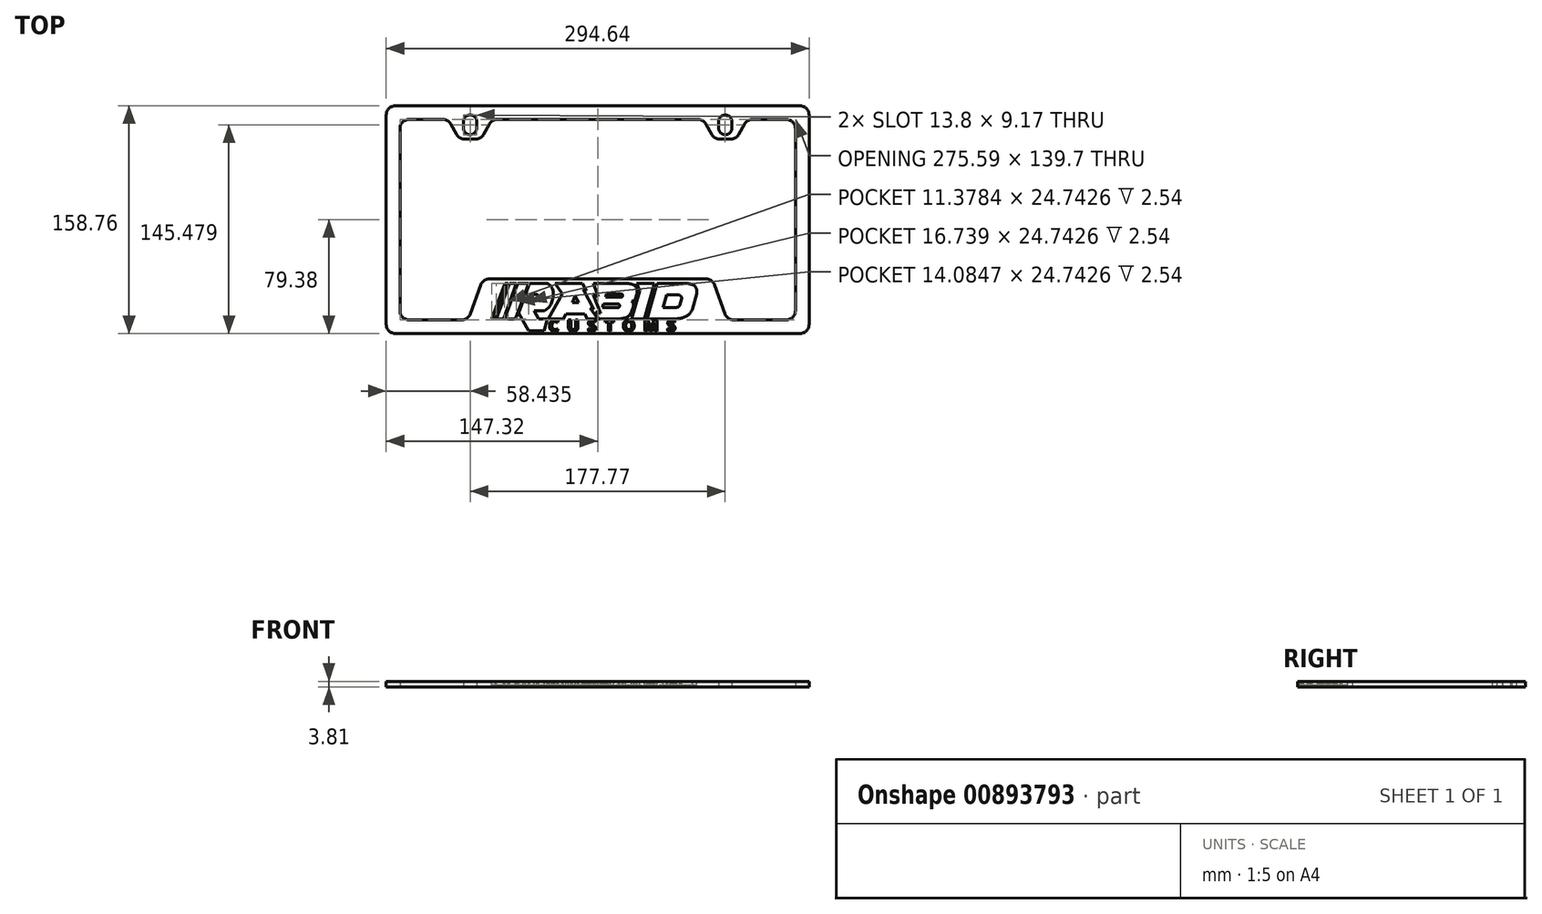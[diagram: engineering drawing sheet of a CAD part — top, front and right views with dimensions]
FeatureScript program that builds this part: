
annotation { "Feature Type Name" : "Feature", "Feature Type Description" : "" }
export const myFeature = defineFeature(function(context is Context, id is Id, definition is map)
    precondition{}
    {
        {
            var Q0;
            Q0=qCreatedBy(makeId("Top.planeOp"),FACE);
            var sketch = newSketch(context, id + "F0", { "sketchPlane" : qUnion([Q0])});
            skLineSegment(sketch, "E0.bottom", {"start": v(-140.97, 79.38) * mm, "end": v(140.97, 79.38) * mm});
            skLineSegment(sketch, "E0.top", {"start": v(-140.97, -79.38) * mm, "end": v(140.97, -79.38) * mm});
            skLineSegment(sketch, "E0.left", {"start": v(-147.32, 73.03) * mm, "end": v(-147.32, -73.03) * mm});
            skLineSegment(sketch, "E0.right", {"start": v(147.32, 73.03) * mm, "end": v(147.32, -73.03) * mm});
            skLineSegment(sketch, "E1.bottom", {"start": v(-131.44, 69.85) * mm, "end": v(-107.87, 69.85) * mm});
            skLineSegment(sketch, "E1.top", {"start": v(-131.44, -69.85) * mm, "end": v(-94.65, -69.85) * mm});
            skLineSegment(sketch, "E1.left", {"start": v(-137.8, 63.5) * mm, "end": v(-137.8, -63.5) * mm});
            skLineSegment(sketch, "E1.right", {"start": v(137.8, 63.5) * mm, "end": v(137.8, -63.5) * mm});
            skLineSegment(sketch, "E2", {"start": v(-102.32, 66.6) * mm, "end": v(-98.34, 59.44) * mm});
            skLineSegment(sketch, "E3", {"start": v(-92.8, 56.19) * mm, "end": v(-85, 56.19) * mm});
            skLineSegment(sketch, "E4", {"start": v(-79.46, 59.44) * mm, "end": v(-75.48, 66.6) * mm});
            skLineSegment(sketch, "E5.trimOffspring", {"start": v(-69.93, 69.85) * mm, "end": v(69.93, 69.85) * mm});
            skArc(sketch, "E6", {"start": v(-84.3, 68.68) * mm, "mid": v(-88.47, 73) * mm, "end": v(-93.37, 69.54) * mm});
            skArc(sketch, "E7", {"start": v(-93.47, 63.22) * mm, "mid": v(-88.82, 59.2) * mm, "end": v(-84.31, 63.37) * mm});
            skLineSegment(sketch, "E8", {"start": v(-93.37, 69.54) * mm, "end": v(-93.47, 63.22) * mm});
            skLineSegment(sketch, "E9", {"start": v(-84.3, 68.68) * mm, "end": v(-84.31, 63.37) * mm});
            skLineSegment(sketch, "E10.MirrorCS", {"start": v(84.3, 68.68) * mm, "end": v(84.31, 63.37) * mm});
            skLineSegment(sketch, "E11.MirrorCS", {"start": v(93.37, 69.54) * mm, "end": v(93.47, 63.22) * mm});
            skLineSegment(sketch, "E12.MirrorCS", {"start": v(102.32, 66.6) * mm, "end": v(98.34, 59.44) * mm});
            skLineSegment(sketch, "E13.MirrorCS", {"start": v(92.8, 56.19) * mm, "end": v(85, 56.19) * mm});
            skLineSegment(sketch, "E14.MirrorCS", {"start": v(79.46, 59.44) * mm, "end": v(75.48, 66.6) * mm});
            skArc(sketch, "E15.MirrorCS", {"start": v(93.47, 63.22) * mm, "mid": v(88.82, 59.2) * mm, "end": v(84.31, 63.37) * mm});
            skArc(sketch, "E16.MirrorCS", {"start": v(84.3, 68.68) * mm, "mid": v(88.47, 73) * mm, "end": v(93.37, 69.54) * mm});
            skLineSegment(sketch, "E17.trimOffspring", {"start": v(107.87, 69.85) * mm, "end": v(131.44, 69.85) * mm});
            skPoint(sketch, "E18.visualSharp", {"position": v(-137.8, 69.85) * mm});
            skArc(sketch, "E18.filletArc", {"start": v(-131.44, 69.85) * mm, "mid": v(-135.94, 68) * mm, "end": v(-137.8, 63.5) * mm});
            skPoint(sketch, "E19.visualSharp", {"position": v(-147.32, 79.38) * mm});
            skArc(sketch, "E19.filletArc", {"start": v(-140.97, 79.37) * mm, "mid": v(-145.46, 77.52) * mm, "end": v(-147.32, 73.03) * mm});
            skPoint(sketch, "E20.visualSharp", {"position": v(137.8, 69.85) * mm});
            skArc(sketch, "E20.filletArc", {"start": v(137.8, 63.5) * mm, "mid": v(135.94, 68) * mm, "end": v(131.44, 69.85) * mm});
            skPoint(sketch, "E21.visualSharp", {"position": v(147.32, 79.38) * mm});
            skArc(sketch, "E21.filletArc", {"start": v(147.32, 73.03) * mm, "mid": v(145.46, 77.52) * mm, "end": v(140.97, 79.38) * mm});
            skPoint(sketch, "E22.visualSharp", {"position": v(147.32, -79.38) * mm});
            skArc(sketch, "E22.filletArc", {"start": v(140.97, -79.37) * mm, "mid": v(145.46, -77.52) * mm, "end": v(147.32, -73.03) * mm});
            skPoint(sketch, "E23.visualSharp", {"position": v(137.8, -69.85) * mm});
            skArc(sketch, "E23.filletArc", {"start": v(131.44, -69.85) * mm, "mid": v(135.94, -68) * mm, "end": v(137.8, -63.5) * mm});
            skPoint(sketch, "E24.visualSharp", {"position": v(-147.32, -79.38) * mm});
            skArc(sketch, "E24.filletArc", {"start": v(-147.32, -73.03) * mm, "mid": v(-145.46, -77.52) * mm, "end": v(-140.97, -79.38) * mm});
            skPoint(sketch, "E25.visualSharp", {"position": v(-137.8, -69.85) * mm});
            skArc(sketch, "E25.filletArc", {"start": v(-137.8, -63.5) * mm, "mid": v(-135.94, -68) * mm, "end": v(-131.44, -69.85) * mm});
            skLineSegment(sketch, "E26", {"start": v(-88.67, -65.63) * mm, "end": v(-81.51, -45.5) * mm});
            skLineSegment(sketch, "E27", {"start": v(-75.53, -41.27) * mm, "end": v(75.53, -41.27) * mm});
            skLineSegment(sketch, "E28", {"start": v(81.51, -45.5) * mm, "end": v(88.67, -65.63) * mm});
            skLineSegment(sketch, "E29.trimOffspring", {"start": v(94.65, -69.85) * mm, "end": v(131.44, -69.85) * mm});
            skPoint(sketch, "E30.visualSharp", {"position": v(-104.14, 69.85) * mm});
            skArc(sketch, "E30.filletArc", {"start": v(-102.32, 66.6) * mm, "mid": v(-104.65, 68.98) * mm, "end": v(-107.87, 69.85) * mm});
            skPoint(sketch, "E31.visualSharp", {"position": v(-96.52, 56.19) * mm});
            skArc(sketch, "E31.filletArc", {"start": v(-98.34, 59.44) * mm, "mid": v(-96, 57.06) * mm, "end": v(-92.8, 56.19) * mm});
            skPoint(sketch, "E32.visualSharp", {"position": v(-81.28, 56.19) * mm});
            skArc(sketch, "E32.filletArc", {"start": v(-85, 56.19) * mm, "mid": v(-81.8, 57.06) * mm, "end": v(-79.46, 59.44) * mm});
            skPoint(sketch, "E33.visualSharp", {"position": v(-73.66, 69.85) * mm});
            skArc(sketch, "E33.filletArc", {"start": v(-69.93, 69.85) * mm, "mid": v(-73.15, 68.98) * mm, "end": v(-75.48, 66.6) * mm});
            skPoint(sketch, "E34.visualSharp", {"position": v(104.14, 69.85) * mm});
            skArc(sketch, "E34.filletArc", {"start": v(107.87, 69.85) * mm, "mid": v(104.65, 68.98) * mm, "end": v(102.32, 66.6) * mm});
            skPoint(sketch, "E35.visualSharp", {"position": v(96.52, 56.19) * mm});
            skArc(sketch, "E35.filletArc", {"start": v(92.8, 56.19) * mm, "mid": v(96, 57.06) * mm, "end": v(98.34, 59.44) * mm});
            skPoint(sketch, "E36.visualSharp", {"position": v(81.28, 56.19) * mm});
            skArc(sketch, "E36.filletArc", {"start": v(79.46, 59.44) * mm, "mid": v(81.8, 57.06) * mm, "end": v(85, 56.19) * mm});
            skPoint(sketch, "E37.visualSharp", {"position": v(73.66, 69.85) * mm});
            skArc(sketch, "E37.filletArc", {"start": v(75.48, 66.6) * mm, "mid": v(73.15, 68.98) * mm, "end": v(69.93, 69.85) * mm});
            skPoint(sketch, "E38.visualSharp", {"position": v(90.17, -69.85) * mm});
            skArc(sketch, "E38.filletArc", {"start": v(88.67, -65.63) * mm, "mid": v(91, -68.69) * mm, "end": v(94.65, -69.85) * mm});
            skPoint(sketch, "E39.visualSharp", {"position": v(80, -41.27) * mm});
            skArc(sketch, "E39.filletArc", {"start": v(81.51, -45.5) * mm, "mid": v(79.19, -42.44) * mm, "end": v(75.53, -41.27) * mm});
            skPoint(sketch, "E40.visualSharp", {"position": v(-80, -41.27) * mm});
            skArc(sketch, "E40.filletArc", {"start": v(-75.53, -41.27) * mm, "mid": v(-79.19, -42.44) * mm, "end": v(-81.51, -45.5) * mm});
            skPoint(sketch, "E41.visualSharp", {"position": v(-90.17, -69.85) * mm});
            skArc(sketch, "E41.filletArc", {"start": v(-94.65, -69.85) * mm, "mid": v(-91, -68.69) * mm, "end": v(-88.67, -65.63) * mm});
            skSolve(sketch);
        }
        {
            var Q0;
            Q0 = qSketchRegion(id + "F0", true);
            extrude(context, id + "F1", {"entities" : qUnion([Q0]), "depth" : 3.8 * mm, "offsetDistance" : 25.4 * mm});
        }
        {
            var Q0;
            Q0=makeQuery(id+"F1.opExtrude","CAP_FACE",FACE,{"disambiguationData":[OSD([sQuery(id+"F0.wireOp",EDGE,"E0.bottom"),sQuery(id+"F0.wireOp",EDGE,"E0.top"),sQuery(id+"F0.wireOp",EDGE,"E0.left"),sQuery(id+"F0.wireOp",EDGE,"E0.right"),sQuery(id+"F0.wireOp",EDGE,"E1.bottom"),sQuery(id+"F0.wireOp",EDGE,"E1.top"),sQuery(id+"F0.wireOp",EDGE,"E1.left"),sQuery(id+"F0.wireOp",EDGE,"E1.right"),sQuery(id+"F0.wireOp",EDGE,"E2"),sQuery(id+"F0.wireOp",EDGE,"E3"),sQuery(id+"F0.wireOp",EDGE,"E4"),sQuery(id+"F0.wireOp",EDGE,"E5.trimOffspring"),sQuery(id+"F0.wireOp",EDGE,"E6"),sQuery(id+"F0.wireOp",EDGE,"E7"),sQuery(id+"F0.wireOp",EDGE,"E8"),sQuery(id+"F0.wireOp",EDGE,"E9"),sQuery(id+"F0.wireOp",EDGE,"E10.MirrorCS"),sQuery(id+"F0.wireOp",EDGE,"E11.MirrorCS"),sQuery(id+"F0.wireOp",EDGE,"E12.MirrorCS"),sQuery(id+"F0.wireOp",EDGE,"E13.MirrorCS"),sQuery(id+"F0.wireOp",EDGE,"E14.MirrorCS"),sQuery(id+"F0.wireOp",EDGE,"E15.MirrorCS"),sQuery(id+"F0.wireOp",EDGE,"E16.MirrorCS"),sQuery(id+"F0.wireOp",EDGE,"E17.trimOffspring"),sQuery(id+"F0.wireOp",EDGE,"E18.filletArc"),sQuery(id+"F0.wireOp",EDGE,"E19.filletArc"),sQuery(id+"F0.wireOp",EDGE,"E20.filletArc"),sQuery(id+"F0.wireOp",EDGE,"E21.filletArc"),sQuery(id+"F0.wireOp",EDGE,"E22.filletArc"),sQuery(id+"F0.wireOp",EDGE,"E23.filletArc"),sQuery(id+"F0.wireOp",EDGE,"E24.filletArc"),sQuery(id+"F0.wireOp",EDGE,"E25.filletArc"),sQuery(id+"F0.wireOp",EDGE,"E26"),sQuery(id+"F0.wireOp",EDGE,"E27"),sQuery(id+"F0.wireOp",EDGE,"E28"),sQuery(id+"F0.wireOp",EDGE,"E29.trimOffspring"),sQuery(id+"F0.wireOp",EDGE,"E30.filletArc"),sQuery(id+"F0.wireOp",EDGE,"E31.filletArc"),sQuery(id+"F0.wireOp",EDGE,"E32.filletArc"),sQuery(id+"F0.wireOp",EDGE,"E33.filletArc"),sQuery(id+"F0.wireOp",EDGE,"E34.filletArc"),sQuery(id+"F0.wireOp",EDGE,"E35.filletArc"),sQuery(id+"F0.wireOp",EDGE,"E36.filletArc"),sQuery(id+"F0.wireOp",EDGE,"E37.filletArc"),sQuery(id+"F0.wireOp",EDGE,"E38.filletArc"),sQuery(id+"F0.wireOp",EDGE,"E39.filletArc"),sQuery(id+"F0.wireOp",EDGE,"E40.filletArc"),sQuery(id+"F0.wireOp",EDGE,"E41.filletArc")])],"isStart":false});
            var sketch = newSketch(context, id + "F2", { "sketchPlane" : qUnion([Q0])});
            skLineSegment(sketch, "E42", {"start": v(61.7, -44.47) * mm, "end": v(41.47, -44.47) * mm});
            skLineSegment(sketch, "E43", {"start": v(-73.67, -69.2) * mm, "end": v(-64.57, -44.47) * mm});
            skLineSegment(sketch, "E44", {"start": v(-57.33, -69.2) * mm, "end": v(-64.96, -69.2) * mm});
            skLineSegment(sketch, "E45", {"start": v(-62.3, -44.47) * mm, "end": v(-71.4, -69.2) * mm});
            skLineSegment(sketch, "E46", {"start": v(-70.7, -69.2) * mm, "end": v(-61.59, -44.47) * mm});
            skLineSegment(sketch, "E47", {"start": v(-56.6, -44.47) * mm, "end": v(-65.71, -69.2) * mm});
            skLineSegment(sketch, "E48", {"start": v(-64.96, -69.2) * mm, "end": v(-55.86, -44.47) * mm});
            skLineSegment(sketch, "E49", {"start": v(-48.22, -44.47) * mm, "end": v(-57.33, -69.2) * mm});
            skLineSegment(sketch, "E50", {"start": v(-50.37, -52.19) * mm, "end": v(-47.53, -44.47) * mm});
            skLineSegment(sketch, "E51", {"start": v(-50.37, -52.19) * mm, "end": v(-42.1, -52.19) * mm});
            skLineSegment(sketch, "E52", {"start": v(-42.54, -56.52) * mm, "end": v(-51.88, -56.52) * mm});
            skLineSegment(sketch, "E53", {"start": v(-51.88, -56.52) * mm, "end": v(-54.97, -64.94) * mm});
            skLineSegment(sketch, "E54", {"start": v(-54.97, -64.94) * mm, "end": v(-48.14, -77.49) * mm});
            skLineSegment(sketch, "E55", {"start": v(-48.14, -77.49) * mm, "end": v(-37.46, -77.49) * mm});
            skLineSegment(sketch, "E56", {"start": v(-37.46, -77.49) * mm, "end": v(-34.94, -69.15) * mm});
            skLineSegment(sketch, "E57", {"start": v(-34.94, -69.15) * mm, "end": v(-41.1, -69.15) * mm});
            skLineSegment(sketch, "E58", {"start": v(-41.1, -69.15) * mm, "end": v(-44.13, -63.59) * mm});
            skLineSegment(sketch, "E59", {"start": v(-44.13, -63.59) * mm, "end": v(-37, -63.59) * mm});
            skLineSegment(sketch, "E60", {"start": v(-34.42, -69.15) * mm, "end": v(-23.93, -69.15) * mm});
            skLineSegment(sketch, "E61", {"start": v(-29.82, -44.47) * mm, "end": v(-24.62, -51.83) * mm});
            skLineSegment(sketch, "E62", {"start": v(-24.62, -51.83) * mm, "end": v(-34.42, -69.15) * mm});
            skLineSegment(sketch, "E63", {"start": v(-23.93, -69.15) * mm, "end": v(-21.93, -65.61) * mm});
            skLineSegment(sketch, "E64", {"start": v(-21.93, -65.61) * mm, "end": v(-9, -65.61) * mm});
            skLineSegment(sketch, "E65", {"start": v(-9, -65.61) * mm, "end": v(-7.24, -69.15) * mm});
            skLineSegment(sketch, "E66", {"start": v(-10.6, -44.47) * mm, "end": v(-7.69, -49.57) * mm});
            skLineSegment(sketch, "E67", {"start": v(-7.69, -49.57) * mm, "end": v(-10.04, -48.69) * mm});
            skLineSegment(sketch, "E68", {"start": v(-10.04, -48.69) * mm, "end": v(-2.75, -62.43) * mm});
            skLineSegment(sketch, "E69", {"start": v(-2.75, -62.43) * mm, "end": v(-5.34, -61.5) * mm});
            skLineSegment(sketch, "E70", {"start": v(-5.34, -61.5) * mm, "end": v(0, -69.15) * mm});
            skLineSegment(sketch, "E71", {"start": v(-13.27, -57.67) * mm, "end": v(-17.73, -57.67) * mm});
            skLineSegment(sketch, "E72", {"start": v(-17.73, -57.67) * mm, "end": v(-15.62, -53.44) * mm});
            skLineSegment(sketch, "E73", {"start": v(-15.62, -53.44) * mm, "end": v(-13.27, -57.67) * mm});
            skLineSegment(sketch, "E74", {"start": v(-3.01, -44.47) * mm, "end": v(0.36, -53.74) * mm});
            skLineSegment(sketch, "E75", {"start": v(0.36, -53.74) * mm, "end": v(-3.05, -52.45) * mm});
            skLineSegment(sketch, "E76", {"start": v(-3.05, -52.45) * mm, "end": v(2.06, -65.37) * mm});
            skLineSegment(sketch, "E77", {"start": v(2.06, -65.37) * mm, "end": v(-1.52, -64.08) * mm});
            skLineSegment(sketch, "E78", {"start": v(-1.52, -64.08) * mm, "end": v(0.42, -69.15) * mm});
            skLineSegment(sketch, "E79", {"start": v(6.17, -51.78) * mm, "end": v(5.5, -54.07) * mm});
            skLineSegment(sketch, "E80", {"start": v(3.42, -61.23) * mm, "end": v(14.32, -61.23) * mm});
            skLineSegment(sketch, "E81", {"start": v(4.12, -58.84) * mm, "end": v(14.59, -58.84) * mm});
            skLineSegment(sketch, "E82", {"start": v(6.17, -51.78) * mm, "end": v(16.81, -51.78) * mm});
            skLineSegment(sketch, "E83", {"start": v(5.5, -54.07) * mm, "end": v(16.55, -54.07) * mm});
            skLineSegment(sketch, "E84", {"start": v(27.03, -44.47) * mm, "end": v(29.34, -49.68) * mm});
            skLineSegment(sketch, "E85", {"start": v(29.34, -49.68) * mm, "end": v(23.7, -69.15) * mm});
            skLineSegment(sketch, "E86", {"start": v(39.6, -44.47) * mm, "end": v(32.55, -69.15) * mm});
            skLineSegment(sketch, "E87", {"start": v(41.47, -44.47) * mm, "end": v(34.41, -69.15) * mm});
            skLineSegment(sketch, "E88", {"start": v(56.09, -52.42) * mm, "end": v(48.07, -52.42) * mm});
            skLineSegment(sketch, "E89", {"start": v(48.07, -52.42) * mm, "end": v(45.58, -61.12) * mm});
            skLineSegment(sketch, "E90", {"start": v(45.58, -61.12) * mm, "end": v(55.1, -61.12) * mm});
            skLineSegment(sketch, "E91", {"start": v(58.55, -55) * mm, "end": v(57.28, -59.47) * mm});
            skFitSpline(sketch, "E92", {"points": [v(69.03, -51.74) * mm, v(69.03, -48.72) * mm, v(67.74, -46.31) * mm, v(65.89, -45.27) * mm, v(61.7, -44.47) * mm], "startDerivative": vector(1.49, 12.2) * mm, "endDerivative": vector(-15.9, 0) * mm});
            skLineSegment(sketch, "E93", {"start": v(69.03, -51.74) * mm, "end": v(66.32, -61.85) * mm});
            skFitSpline(sketch, "E94", {"points": [v(23.6, -56.8) * mm, v(25, -56.49) * mm, v(25.96, -55.52) * mm, v(27.52, -50.22) * mm, v(27.14, -47.73) * mm, v(26.08, -46.24) * mm, v(23.9, -45.04) * mm, v(20.5, -44.47) * mm], "startDerivative": vector(13.14, 2.22) * mm, "endDerivative": vector(-18.26, 0) * mm});
            skFitSpline(sketch, "E95", {"points": [v(23.6, -56.8) * mm, v(24.49, -57.51) * mm, v(25.04, -58.8) * mm, v(24.95, -60.03) * mm, v(23.07, -65.26) * mm, v(21.6, -67.05) * mm, v(19.9, -68.2) * mm, v(17.8, -68.74) * mm, v(14.68, -69.15) * mm], "startDerivative": vector(10.68, -6.55) * mm, "endDerivative": vector(-22.08, 0) * mm});
            skFitSpline(sketch, "E96", {"points": [v(16.81, -51.78) * mm, v(17.08, -51.92) * mm, v(17.3, -52.27) * mm, v(17.17, -53.62) * mm, v(17.02, -53.9) * mm, v(16.55, -54.07) * mm], "startDerivative": vector(2, 0) * mm, "endDerivative": vector(-2.92, 0) * mm});
            skFitSpline(sketch, "E97", {"points": [v(14.59, -58.84) * mm, v(14.93, -58.98) * mm, v(15.18, -59.4) * mm, v(15.19, -60.58) * mm, v(14.97, -60.97) * mm, v(14.32, -61.23) * mm], "startDerivative": vector(2.42, 0) * mm, "endDerivative": vector(-5.66, -0.58) * mm});
            skFitSpline(sketch, "E98", {"points": [v(-35.16, -44.47) * mm, v(-33.3, -45.6) * mm, v(-31.9, -47.56) * mm, v(-30.92, -50.87) * mm, v(-31.1, -54.42) * mm, v(-32.18, -58.24) * mm, v(-34.28, -61.37) * mm, v(-37, -63.59) * mm], "startDerivative": vector(16.87, -8.46) * mm, "endDerivative": vector(-19.03, -13.81) * mm});
            skFitSpline(sketch, "E99", {"points": [v(56.09, -52.42) * mm, v(56.97, -52.62) * mm, v(57.66, -53.03) * mm, v(58.2, -53.64) * mm, v(58.55, -55) * mm], "startDerivative": vector(3.62, 0) * mm, "endDerivative": vector(-0.87, -7.03) * mm});
            skFitSpline(sketch, "E100", {"points": [v(55.1, -61.12) * mm, v(55.87, -60.94) * mm, v(56.58, -60.66) * mm, v(57.03, -60.13) * mm, v(57.28, -59.47) * mm], "startDerivative": vector(2.97, 0.66) * mm, "endDerivative": vector(0.87, 2.77) * mm});
            skLineSegment(sketch, "E101.trimOffspring", {"start": v(-62.3, -44.47) * mm, "end": v(-64.57, -44.47) * mm});
            skLineSegment(sketch, "E102.trimOffspring", {"start": v(-56.6, -44.47) * mm, "end": v(-61.59, -44.47) * mm});
            skLineSegment(sketch, "E103.trimOffspring", {"start": v(-48.22, -44.47) * mm, "end": v(-55.86, -44.47) * mm});
            skLineSegment(sketch, "E104.trimOffspring", {"start": v(-35.16, -44.47) * mm, "end": v(-47.53, -44.47) * mm});
            skLineSegment(sketch, "E105.trimOffspring", {"start": v(-65.71, -69.2) * mm, "end": v(-70.7, -69.2) * mm});
            skLineSegment(sketch, "E106.trimOffspring", {"start": v(-71.4, -69.2) * mm, "end": v(-73.67, -69.2) * mm});
            skLineSegment(sketch, "E107.trimOffspring", {"start": v(-7.24, -69.15) * mm, "end": v(0, -69.15) * mm});
            skLineSegment(sketch, "E108.trimOffspring", {"start": v(0.42, -69.15) * mm, "end": v(14.68, -69.15) * mm});
            skLineSegment(sketch, "E109.trimOffspring", {"start": v(-10.6, -44.47) * mm, "end": v(-29.82, -44.47) * mm});
            skLineSegment(sketch, "E110.trimOffspring", {"start": v(4.12, -58.84) * mm, "end": v(3.42, -61.23) * mm});
            skLineSegment(sketch, "E111.trimOffspring", {"start": v(20.5, -44.47) * mm, "end": v(-3.01, -44.47) * mm});
            skLineSegment(sketch, "E112.trimOffspring", {"start": v(23.7, -69.15) * mm, "end": v(32.55, -69.15) * mm});
            skLineSegment(sketch, "E113.trimOffspring", {"start": v(34.41, -69.15) * mm, "end": v(54.45, -69.15) * mm});
            skLineSegment(sketch, "E114.trimOffspring", {"start": v(39.6, -44.47) * mm, "end": v(27.03, -44.47) * mm});
            skFitSpline(sketch, "E115", {"points": [v(66.32, -61.85) * mm, v(65.54, -63.56) * mm, v(64.28, -65.35) * mm, v(62.43, -66.9) * mm, v(60.42, -67.97) * mm, v(58.05, -68.65) * mm, v(54.45, -69.15) * mm], "startDerivative": vector(-4.85, -11.73) * mm, "endDerivative": vector(-18.79, 0) * mm});
            skFitSpline(sketch, "E116", {"points": [v(-42.1, -52.19) * mm, v(-41.42, -53.19) * mm, v(-41.46, -54.6) * mm, v(-42.1, -56.1) * mm, v(-42.54, -56.52) * mm], "startDerivative": vector(3.26, -3.69) * mm, "endDerivative": vector(-2.46, -1.8) * mm});
            skText(sketch, "E117", { "text": "C  U  S  T  O  M  S", "fontName": "OpenSans-Bold.ttf"});
            const initialGuessF2  = {"E117": [-0.03424, -0.07786, 1, 0, 0.00805]};
            skSetInitialGuess(sketch, initialGuessF2);
            skSolve(sketch);
        }
        {
            var Q0;
            Q0 = qSketchRegion(id + "F2", true);
            extrude(context, id + "F3", {"entities" : qUnion([Q0]), "operationType" : NewBodyOperationType.REMOVE, "oppositeDirection" : true, "depth" : 2.54 * mm, "offsetDistance" : 25.4 * mm});
        }
    });
